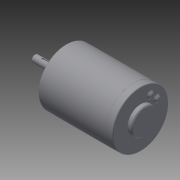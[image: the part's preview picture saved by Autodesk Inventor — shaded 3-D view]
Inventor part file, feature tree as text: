
AUTODESK INVENTOR PART (.ipt)
format: ipt  version: 2014 SP1 (Build 180222100, 222)  size: 161,280 bytes
history: native  units: in
note: dims shown in document units (in); Inventor stores cm internally (conversion verified against a paired STEP export)
features: chamfer x1, other x1, imported_body x1
ambient origin geometry x8: Origin, YZ Plane, XZ Plane, XY Plane, X Axis, Y Axis, Z Axis, Center Point
bodies: Body1 (feature_tree)
feature tree (3):
  chamfer  "Chamfer3"  [1 undecoded]
  other  "217-3371-STEP1"
  imported_body  "Base1"
note: 1 required parameter value undecoded (feature->parameter linkage not recoverable at this tier; creation-order binding heuristic only, values carry confidence <= 0.55)
